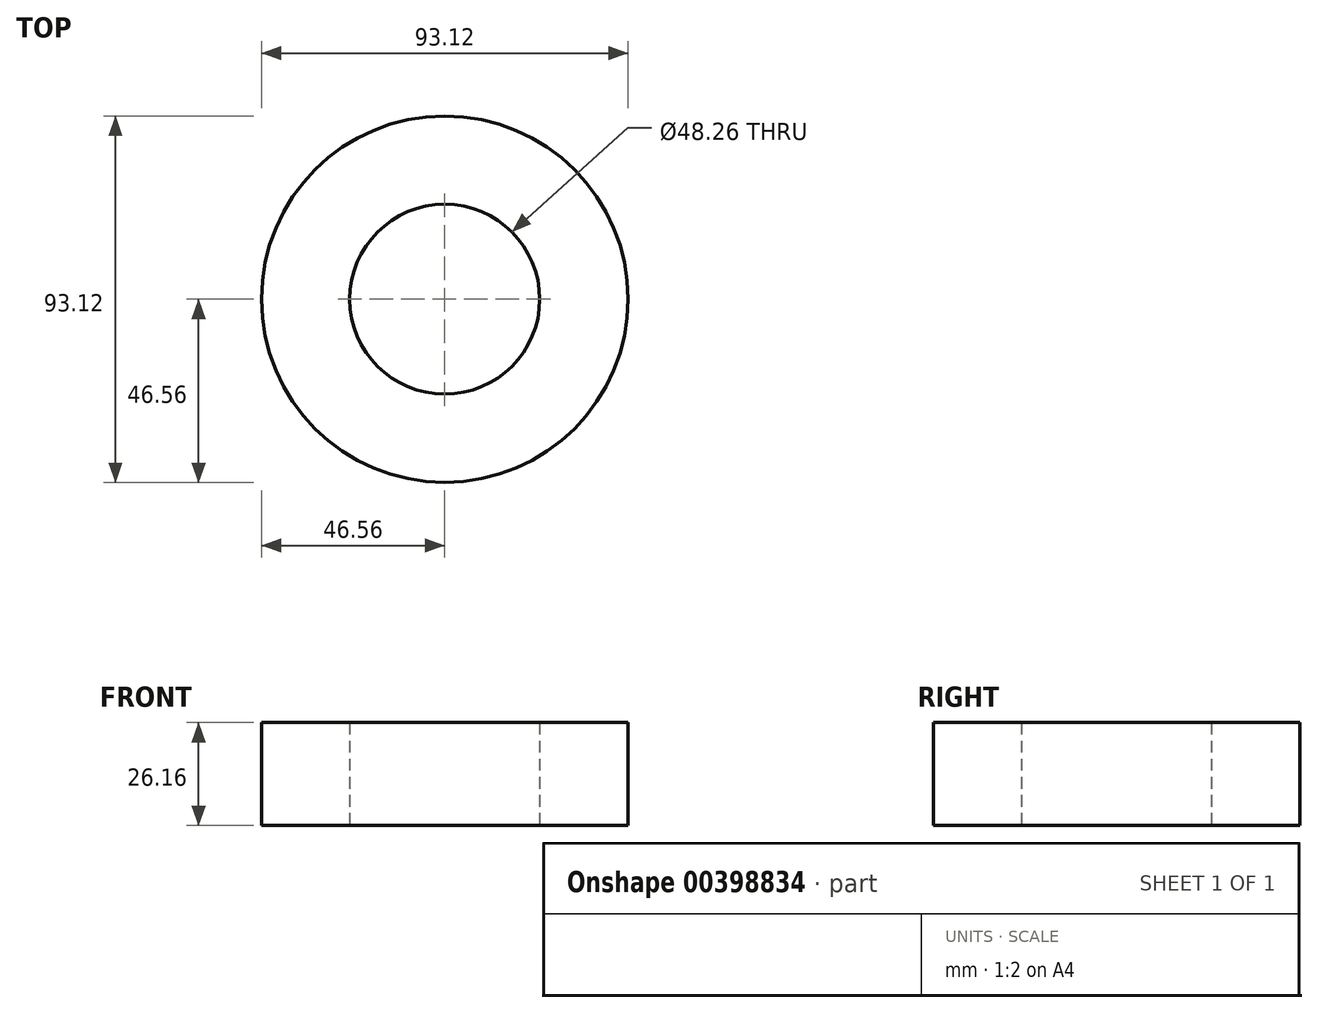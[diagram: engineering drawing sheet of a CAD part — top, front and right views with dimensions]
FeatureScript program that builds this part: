
annotation { "Feature Type Name" : "Feature", "Feature Type Description" : "" }
export const myFeature = defineFeature(function(context is Context, id is Id, definition is map)
    precondition{}
    {
        {
            var Q0;
            Q0=qCreatedBy(makeId("Top.planeOp"),FACE);
            var sketch = newSketch(context, id + "F0", { "sketchPlane" : qUnion([Q0])});
            skCircle(sketch, "E0", {"center": v(0, 0) * mm, "radius": 46.56 * mm});
            skCircle(sketch, "E1", {"center": v(0, 0) * mm, "radius": 24.13 * mm});
            skSolve(sketch);
        }
        {
            var Q0;
            Q0 = qSketchRegion(id + "F0", true);
            extrude(context, id + "F1", {"entities" : qUnion([Q0]), "depth" : 26.16 * mm});
        }
    });
